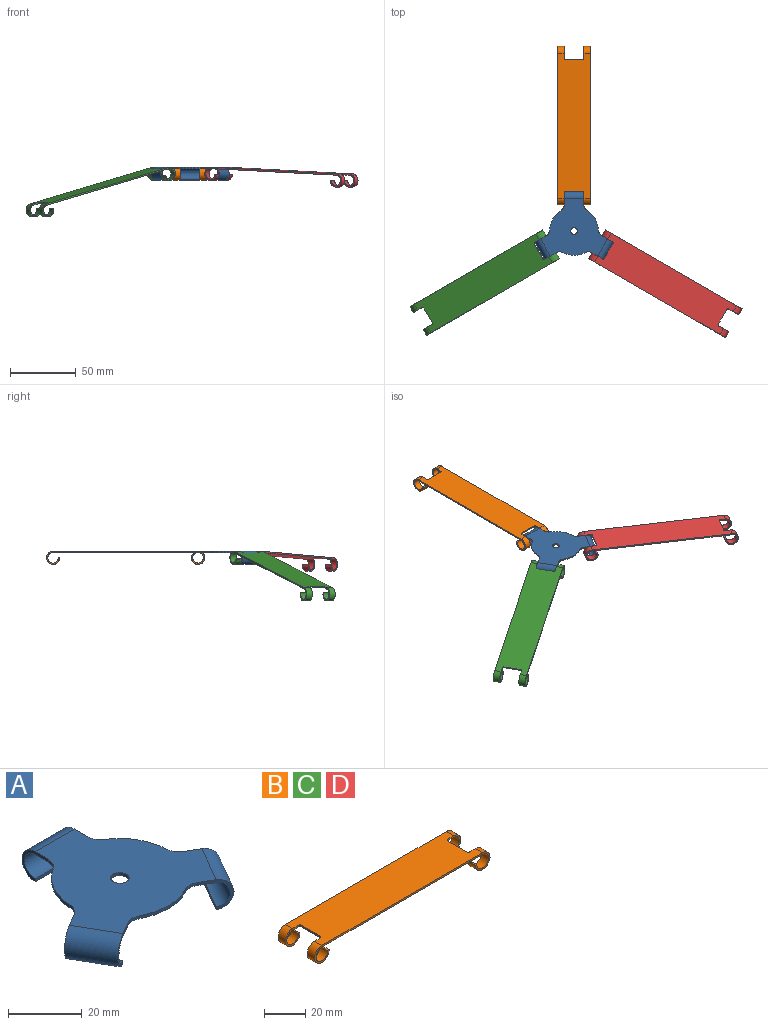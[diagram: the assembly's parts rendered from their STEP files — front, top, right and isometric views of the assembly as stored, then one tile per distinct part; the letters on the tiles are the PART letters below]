
ASSEMBLY  parts=4 mates=3
PART A: 27 faces, bbox 59.5x51.5x10 mm
  f0: cylinder r=18.5mm len=14.98mm, axis (0,0,1), area 18mm2, adj f12,f16,f20,f25
  f1: plane 10x8.75mm, normal (0.5,0.87,0), area 19.2mm2, adj f10,f12,f15,f16,f19,f25
  f2: plane 10x8.75mm, normal (-0.5,-0.87,0), area 19.2mm2, adj f10,f12,f15,f16,f19,f24
  f3: cylinder r=18.5mm len=17.29mm, axis (0,0,1), area 18mm2, adj f12,f16,f23,f24
  f4: plane 10x8.75mm, normal (0.5,-0.87,0), area 19.2mm2, adj f9,f12,f14,f16,f18,f23
  f5: plane 10x8.75mm, normal (-0.5,0.87,0), area 19.2mm2, adj f9,f12,f14,f16,f18,f22
  f6: cylinder r=18.5mm len=14.98mm, axis (0,0,1), area 18mm2, adj f12,f16,f21,f22
  f7: plane 10.1x10mm, normal (-1,0,0), area 19.2mm2, adj f11,f12,f13,f16,f17,f21
  f8: plane 10.1x10mm, normal (1,0,0), area 19.2mm2, adj f11,f12,f13,f16,f17,f20
  f9: plane 12.99x7.5mm, normal (0.87,0.5,0), area 15mm2, adj f4,f5,f14,f18
  f10: plane 12.99x7.5mm, normal (-0.87,0.5,0), area 15mm2, adj f1,f2,f15,f19
  f11: plane 15x1mm, normal (0,-1,0), area 15mm2, adj f7,f8,f13,f17
  f12: plane 50.8x44mm, normal (0,0,1), area 1379.7mm2, adj f0,f1,f2,f3,f4,f5,f6,f7
  f13: cylinder r=5mm len=15mm, axis (1,0,0), area 235.6mm2, adj f7,f8,f11,f12
  f14: cylinder r=5mm len=15.49mm, axis (-0.5,0.87,0), area 235.6mm2, adj f4,f5,f9,f12
  f15: cylinder r=5mm len=15.49mm, axis (-0.5,-0.87,0), area 235.6mm2, adj f1,f2,f10,f12
  f16: plane 50.8x44mm, normal (0,0,-1), area 1379.7mm2, adj f0,f1,f2,f3,f4,f5,f6,f7
  f17: cylinder r=4mm len=15mm, axis (1,0,0), area 188.5mm2, adj f7,f8,f11,f16
  f18: cylinder r=4mm len=14.99mm, axis (-0.5,0.87,0), area 188.5mm2, adj f4,f5,f9,f16
  f19: cylinder r=4mm len=14.99mm, axis (-0.5,-0.87,0), area 188.5mm2, adj f1,f2,f10,f16
  f20: cylinder r=5mm len=4.23mm, axis (0,0,1), area 5mm2, adj f0,f8,f12,f16
  f21: cylinder r=5mm len=4.23mm, axis (0,0,1), area 5mm2, adj f6,f7,f12,f16
  f22: cylinder r=5mm len=4.14mm, axis (0,0,1), area 5mm2, adj f5,f6,f12,f16
  f23: cylinder r=5mm len=4.84mm, axis (0,0,1), area 5mm2, adj f3,f4,f12,f16
  f24: cylinder r=5mm len=4.84mm, axis (0,0,1), area 5mm2, adj f2,f3,f12,f16
  f25: cylinder r=5mm len=4.14mm, axis (0,0,1), area 5mm2, adj f0,f1,f12,f16
  f26: cylinder r=2.5mm len=5mm, axis (0,0,1), area 15.7mm2, adj f12,f16
PART B: 26 faces, bbox 120x25x10 mm
  f0: cylinder r=4mm len=8mm, axis (0,1,0), area 94.2mm2, adj f1,f7,f15,f17
  f1: plane 110x25mm, normal (0,0,-1), area 2600.9mm2, adj f0,f2,f8,f9,f14,f15,f16,f17
  f2: cylinder r=4mm len=8mm, axis (0,1,0), area 94.2mm2, adj f1,f3,f14,f20
  f3: plane 5x1mm, normal (0,0,1), area 5mm2, adj f2,f4,f14,f20
  f4: cylinder r=5mm len=10mm, axis (0,1,0), area 117.8mm2, adj f3,f5,f14,f20
  f5: plane 110x25mm, normal (0,0,1), area 2600.9mm2, adj f4,f6,f11,f12,f14,f15,f16,f17
  f6: cylinder r=5mm len=10mm, axis (0,1,0), area 117.8mm2, adj f5,f7,f15,f17
  f7: plane 5x1mm, normal (0,0,1), area 5mm2, adj f0,f6,f15,f17
  f8: cylinder r=4mm len=8mm, axis (0,1,0), area 94.2mm2, adj f1,f13,f14,f18
  f9: cylinder r=4mm len=8mm, axis (0,1,0), area 94.2mm2, adj f1,f10,f15,f19
  f10: plane 5x1mm, normal (0,0,1), area 5mm2, adj f9,f11,f15,f19
  f11: cylinder r=5mm len=10mm, axis (0,1,0), area 117.8mm2, adj f5,f10,f15,f19
  f12: cylinder r=5mm len=10mm, axis (0,1,0), area 117.8mm2, adj f5,f13,f14,f18
  f13: plane 5x1mm, normal (0,0,1), area 5mm2, adj f8,f12,f14,f18
  f14: plane 120x10mm, normal (0,-1,0), area 152.4mm2, adj f1,f2,f3,f4,f5,f8,f12,f13
  f15: plane 120x10mm, normal (0,1,0), area 152.4mm2, adj f0,f1,f5,f6,f7,f9,f10,f11
  f16: plane 13x1mm, normal (-1,0,0), area 13mm2, adj f1,f5,f24,f25
  f17: plane 10x10mm, normal (0,-1,0), area 25.2mm2, adj f0,f1,f5,f6,f7,f25
  f18: plane 10x10mm, normal (0,1,0), area 25.2mm2, adj f1,f5,f8,f12,f13,f24
  f19: plane 10x10mm, normal (0,-1,0), area 25.2mm2, adj f1,f5,f9,f10,f11,f22
  f20: plane 10x10mm, normal (0,1,0), area 25.2mm2, adj f1,f2,f3,f4,f5,f23
  f21: plane 13x1mm, normal (1,0,0), area 13mm2, adj f1,f5,f22,f23
  f22: cylinder r=1mm len=1mm, axis (0,0,-1), area 1.6mm2, adj f1,f5,f19,f21
  f23: cylinder r=1mm len=1mm, axis (0,0,1), area 1.6mm2, adj f1,f5,f20,f21
  f24: cylinder r=1mm len=1mm, axis (0,0,1), area 1.6mm2, adj f1,f5,f16,f18
  f25: cylinder r=1mm len=1mm, axis (0,0,-1), area 1.6mm2, adj f1,f5,f16,f17
PART C: same geometry as B
PART D: same geometry as B
PLACE A at identity fixed
PLACE B rot(axis=(0,0,-1),90deg) t=(0,30,0)mm
PLACE C rot(axis=(0.11,-0.43,0.9),33.3deg) t=(-68.85,-89.75,-13.96)mm
PLACE D rot(axis=(0.02,0.09,-1),30.1deg) t=(69.43,-90.09,-2.53)mm
MATE revolute A.f15 <-> D.f0  axis (0.5,0.87,0) through (17.9,-69,-5)mm
MATE revolute B.f2 <-> A.f13  axis (1,0,0) through (-7.5,-25,-5)mm
MATE revolute C.f2 <-> A.f14  axis (-0.5,0.87,0) through (-25.4,-56,-5)mm
